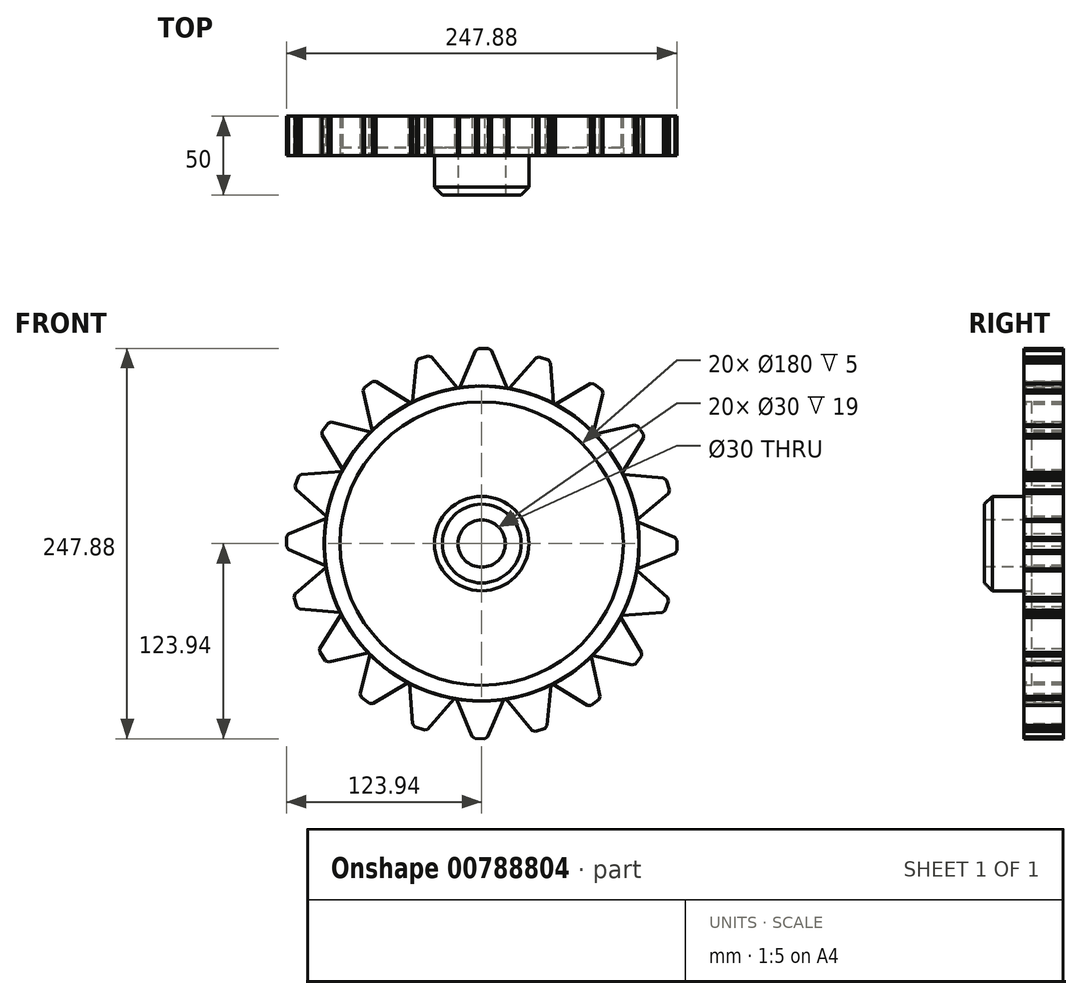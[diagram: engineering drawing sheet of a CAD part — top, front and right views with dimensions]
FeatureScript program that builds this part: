
annotation { "Feature Type Name" : "Feature", "Feature Type Description" : "" }
export const myFeature = defineFeature(function(context is Context, id is Id, definition is map)
    precondition{}
    {
        {
            var Q0;
            Q0=qCreatedBy(makeId("Front.planeOp"),FACE);
            var sketch = newSketch(context, id + "F0", { "sketchPlane" : qUnion([Q0])});
            skCircle(sketch, "E0", {"center": v(0, 0) * mm, "radius": 100 * mm});
            skSolve(sketch);
        }
        {
            var Q0;
            Q0=makeQuery(id+"F0.imprint","IMPRINT",FACE,{"disambiguationData":[TD([[makeQuery(id+"F0.imprint","IMPRINT",EDGE,{"derivedFrom":sQuery(id+"F0.wireOp",EDGE,"E0")}),1.0]])]});
            extrude(context, id + "F1", {"entities" : qUnion([Q0]), "depth" : 25 * mm, "offsetDistance" : 25 * mm});
        }
        {
            var Q0;
            Q0=makeQuery(id+"F1.opExtrude","CAP_FACE",FACE,{"disambiguationData":[OSD([sQuery(id+"F0.wireOp",EDGE,"E0")])],"isStart":false});
            var sketch = newSketch(context, id + "F2", { "sketchPlane" : qUnion([Q0])});
            skLineSegment(sketch, "E1", {"start": v(17.27, 98.5) * mm, "end": v(45.71, 88.94) * mm});
            skLineSegment(sketch, "E2", {"start": v(17.27, 98.5) * mm, "end": v(35.2, 118.9) * mm});
            skLineSegment(sketch, "E3", {"start": v(35.2, 118.9) * mm, "end": v(43.73, 116.03) * mm});
            skLineSegment(sketch, "E4", {"start": v(43.73, 116.03) * mm, "end": v(45.71, 88.94) * mm});
            skSolve(sketch);
        }
        {
            var Q0;
            {var subQ0=sQuery(id+"F2.wireOp",EDGE,"E2");Q0=makeQuery(id+"F2.imprint","IMPRINT",FACE,{"disambiguationData":[TD([[makeQuery(id+"F2.imprint","IMPRINT",EDGE,{"derivedFrom":subQ0}),-1.0]])]});}
            var Q1;
            {var subQ0=sQuery(id+"F2.wireOp",EDGE,"E1");Q1=makeQuery(id+"F2.imprint","IMPRINT",FACE,{"disambiguationData":[TD([[makeQuery(id+"F2.imprint","IMPRINT",EDGE,{"derivedFrom":subQ0}),-1.0]])]});}
            extrude(context, id + "F3", {"entities" : qUnion([Q0, Q1]), "operationType" : NewBodyOperationType.ADD, "oppositeDirection" : true, "depth" : 25 * mm, "offsetDistance" : 25 * mm});
        }
        {
            var Q0;
            Q0=makeQuery(id+"F3.opExtrude","SWEPT_EDGE",EDGE,{"disambiguationData":[OSD([sQuery(id+"F0.wireOp",EDGE,"E0"),sQuery(id+"F2.wireOp",EDGE,"E1"),sQuery(id+"F2.wireOp",EDGE,"E2")])]});
            var Q1;
            Q1=makeQuery(id+"F3.opExtrude","SWEPT_EDGE",EDGE,{"disambiguationData":[OSD([sQuery(id+"F0.wireOp",EDGE,"E0"),sQuery(id+"F2.wireOp",EDGE,"E1"),sQuery(id+"F2.wireOp",EDGE,"E4")])]});
            fillet(context, id + "F4", {"entities" : qUnion([Q0, Q1]), "radius" : 5 * mm, "tangentPropagation" : true, "allowEdgeOverflow" : false});
        }
        {
            var Q0;
            Q0=makeQuery(id+"F3.opExtrude","SWEPT_EDGE",EDGE,{"disambiguationData":[OSD([sQuery(id+"F2.wireOp",EDGE,"E2"),sQuery(id+"F2.wireOp",EDGE,"E3")])]});
            var Q1;
            Q1=makeQuery(id+"F3.opExtrude","SWEPT_EDGE",EDGE,{"disambiguationData":[OSD([sQuery(id+"F2.wireOp",EDGE,"E3"),sQuery(id+"F2.wireOp",EDGE,"E4")])]});
            chamfer(context, id + "F5", {"entities" : qUnion([Q0, Q1]), "width" : 2 * mm, "tangentPropagation" : true});
        }
        {
            var Q0;
            Q0=makeQuery(id+"F1.opExtrude","SWEPT_BODY",BODY,{"disambiguationData":[OSD([sQuery(id+"F0.wireOp",EDGE,"E0")])]});
            var Q1;
            Q1=makeQuery(id+"F1.opExtrude","SWEPT_FACE",FACE,{"disambiguationData":[OSD([sQuery(id+"F0.wireOp",EDGE,"E0")])]});
            circularPattern(context, id + "F6", {"entities" : qUnion([Q0]), "axis" : qUnion([Q1]), "angle" : 360 * degree, "instanceCount" : 20, "equalSpace" : true});
        }
        {
            var Q0;
            {var subQ0=sQuery(id+"F0.wireOp",EDGE,"E0");Q0=makeQuery(id+"F6.opPattern","COPY",FACE,{"derivedFrom":makeQuery(id+"F3.boolean.opBoolean","MERGE",FACE,{"derivedFrom":[makeQuery(id+"F1.opExtrude","CAP_FACE",FACE,{"disambiguationData":[OSD([subQ0])],"isStart":false}),makeQuery(id+"F3.opExtrude","CAP_FACE",FACE,{"disambiguationData":[OSD([subQ0,sQuery(id+"F2.wireOp",EDGE,"E2"),sQuery(id+"F2.wireOp",EDGE,"E3"),sQuery(id+"F2.wireOp",EDGE,"E4")])],"isStart":true})]}),"instanceName":"16"});}
            var sketch = newSketch(context, id + "F7", { "sketchPlane" : qUnion([Q0])});
            skCircle(sketch, "E5", {"center": v(0, 0) * mm, "radius": 90 * mm});
            skSolve(sketch);
        }
        {
            var Q0;
            Q0=makeQuery(id+"F7.imprint","IMPRINT",FACE,{"disambiguationData":[TD([[makeQuery(id+"F7.imprint","IMPRINT",EDGE,{"derivedFrom":sQuery(id+"F7.wireOp",EDGE,"E5")}),1.0]])]});
            extrude(context, id + "F8", {"entities" : qUnion([Q0]), "operationType" : NewBodyOperationType.REMOVE, "oppositeDirection" : true, "depth" : 5 * mm, "offsetDistance" : 25 * mm});
        }
        {
            var Q0;
            Q0=makeQuery(id+"F8.boolean.opBoolean","COPY",FACE,{"disambiguationData":[OD(0.0)],"derivedFrom":makeQuery(id+"F8.opExtrude","CAP_FACE",FACE,{"disambiguationData":[OSD([sQuery(id+"F7.wireOp",EDGE,"E5")])],"isStart":false})});
            var sketch = newSketch(context, id + "F9", { "sketchPlane" : qUnion([Q0])});
            skCircle(sketch, "E6", {"center": v(0, 0) * mm, "radius": 30 * mm});
            skSolve(sketch);
        }
        {
            var Q0;
            Q0=makeQuery(id+"F9.imprint","IMPRINT",FACE,{"disambiguationData":[TD([[makeQuery(id+"F9.imprint","IMPRINT",EDGE,{"derivedFrom":sQuery(id+"F9.wireOp",EDGE,"E6")}),1.0]])]});
            extrude(context, id + "F10", {"entities" : qUnion([Q0]), "depth" : 30 * mm, "offsetDistance" : 25 * mm});
        }
        {
            var Q0;
            Q0=makeQuery(id+"F10.opExtrude","CAP_FACE",FACE,{"disambiguationData":[OSD([sQuery(id+"F9.wireOp",EDGE,"E6")])],"isStart":false});
            var sketch = newSketch(context, id + "F11", { "sketchPlane" : qUnion([Q0])});
            skCircle(sketch, "E7", {"center": v(0, 0) * mm, "radius": 15 * mm});
            skSolve(sketch);
        }
        {
            var Q0;
            Q0=makeQuery(id+"F11.imprint","IMPRINT",FACE,{"disambiguationData":[TD([[makeQuery(id+"F11.imprint","IMPRINT",EDGE,{"derivedFrom":sQuery(id+"F11.wireOp",EDGE,"E7")}),1.0]])]});
            extrude(context, id + "F12", {"entities" : qUnion([Q0]), "operationType" : NewBodyOperationType.REMOVE, "oppositeDirection" : true, "depth" : 49 * mm, "offsetDistance" : 25 * mm});
        }
        {
            var Q0;
            Q0=makeQuery(id+"F10.opExtrude","CAP_EDGE",EDGE,{"disambiguationData":[OSD([sQuery(id+"F9.wireOp",EDGE,"E6")])],"isStart":false});
            var Q1;
            Q1=makeQuery(id+"F12.boolean.opBoolean","COPY",EDGE,{"derivedFrom":makeQuery(id+"F12.opExtrude","CAP_EDGE",EDGE,{"disambiguationData":[OSD([sQuery(id+"F11.wireOp",EDGE,"E7")])],"isStart":true})});
            chamfer(context, id + "F13", {"entities" : qUnion([Q0, Q1]), "width" : 5 * mm, "tangentPropagation" : true});
        }
    });
